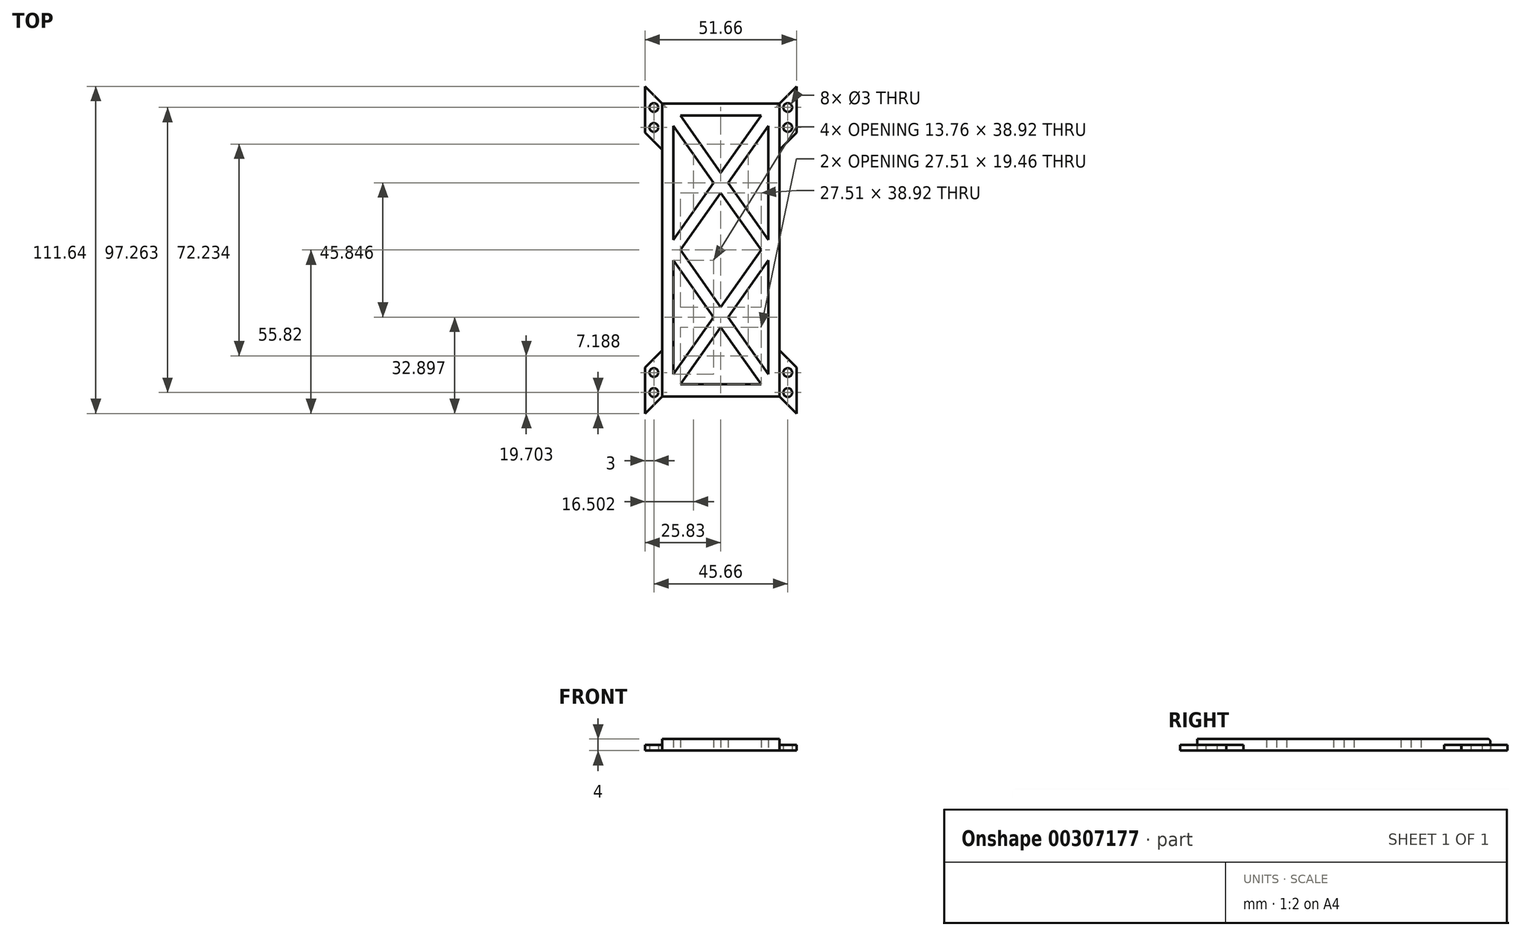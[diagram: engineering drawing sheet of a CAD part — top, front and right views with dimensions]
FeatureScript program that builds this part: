
annotation { "Feature Type Name" : "Feature", "Feature Type Description" : "" }
export const myFeature = defineFeature(function(context is Context, id is Id, definition is map)
    precondition{}
    {
        {
            var Q0;
            Q0=qCreatedBy(makeId("Top.planeOp"),FACE);
            var sketch = newSketch(context, id + "F0", { "sketchPlane" : qUnion([Q0])});
            skLineSegment(sketch, "E0.bottom", {"start": v(20, 50) * mm, "end": v(-20, 50) * mm});
            skLineSegment(sketch, "E0.top", {"start": v(20, -50) * mm, "end": v(-20, -50) * mm});
            skLineSegment(sketch, "E0.left", {"start": v(20, 50) * mm, "end": v(20, -50) * mm});
            skLineSegment(sketch, "E0.right", {"start": v(-20, 50) * mm, "end": v(-20, -50) * mm});
            skPoint(sketch, "E0.middle", {"position": v(0, 0) * mm});
            skLineSegment(sketch, "E1.bottom", {"start": v(16.2, -45.85) * mm, "end": v(-16.2, -45.85) * mm});
            skLineSegment(sketch, "E1.top", {"start": v(16.2, 45.85) * mm, "end": v(-16.2, 45.85) * mm});
            skLineSegment(sketch, "E1.left", {"start": v(16.2, -45.85) * mm, "end": v(16.2, 45.85) * mm});
            skLineSegment(sketch, "E1.right", {"start": v(-16.2, -45.85) * mm, "end": v(-16.2, 45.85) * mm});
            skLineSegment(sketch, "E2", {"start": v(-16.2, 0) * mm, "end": v(16.2, 0) * mm});
            skLineSegment(sketch, "E3", {"start": v(16.2, 0) * mm, "end": v(-16.2, 45.85) * mm});
            skLineSegment(sketch, "E4", {"start": v(-16.2, 0) * mm, "end": v(16.2, 45.85) * mm});
            skLineSegment(sketch, "E5", {"start": v(-16.2, 0) * mm, "end": v(16.2, -45.85) * mm});
            skLineSegment(sketch, "E6", {"start": v(16.2, 0) * mm, "end": v(-16.2, -45.85) * mm});
            skLineSegment(sketch, "E7.0", {"start": v(17.84, 1.15) * mm, "end": v(-14.57, 47) * mm});
            skLineSegment(sketch, "E8.0", {"start": v(14.57, -1.15) * mm, "end": v(-17.84, 44.7) * mm});
            skLineSegment(sketch, "E9.0", {"start": v(-14.57, -1.15) * mm, "end": v(17.84, 44.7) * mm});
            skLineSegment(sketch, "E10.0", {"start": v(-17.84, 1.15) * mm, "end": v(14.57, 47) * mm});
            skLineSegment(sketch, "E11.0", {"start": v(-16.2, -2) * mm, "end": v(16.2, -2) * mm});
            skLineSegment(sketch, "E12.0", {"start": v(-16.2, 2) * mm, "end": v(16.2, 2) * mm});
            skLineSegment(sketch, "E13.0", {"start": v(14.57, 1.15) * mm, "end": v(-17.84, -44.7) * mm});
            skLineSegment(sketch, "E14.0", {"start": v(17.84, -1.15) * mm, "end": v(-14.57, -47) * mm});
            skLineSegment(sketch, "E15.0", {"start": v(-17.84, -1.15) * mm, "end": v(14.57, -47) * mm});
            skLineSegment(sketch, "E16.0", {"start": v(-14.57, 1.15) * mm, "end": v(17.84, -44.7) * mm});
            skLineSegment(sketch, "E17", {"start": v(20, 50) * mm, "end": v(25.83, 55.82) * mm});
            skLineSegment(sketch, "E18", {"start": v(25.83, 55.82) * mm, "end": v(25.83, 40.05) * mm});
            skLineSegment(sketch, "E19", {"start": v(25.83, 40.05) * mm, "end": v(20, 34.24) * mm});
            skLineSegment(sketch, "E20.MirrorCS", {"start": v(25.83, -40.05) * mm, "end": v(20, -34.24) * mm});
            skLineSegment(sketch, "E21.MirrorCS", {"start": v(25.83, -55.82) * mm, "end": v(25.83, -40.05) * mm});
            skLineSegment(sketch, "E22.MirrorCS", {"start": v(20, -50) * mm, "end": v(25.83, -55.82) * mm});
            skLineSegment(sketch, "E23", {"start": v(0, 50) * mm, "end": v(0, -45.85) * mm, "construction": true});
            skLineSegment(sketch, "E24.MirrorCS", {"start": v(-25.83, 40.05) * mm, "end": v(-20, 34.24) * mm});
            skLineSegment(sketch, "E25.MirrorCS", {"start": v(-25.83, 55.82) * mm, "end": v(-25.83, 40.05) * mm});
            skLineSegment(sketch, "E26.MirrorCS", {"start": v(-20, 50) * mm, "end": v(-25.83, 55.82) * mm});
            skLineSegment(sketch, "E27.MirrorCS", {"start": v(-25.83, -40.05) * mm, "end": v(-20, -34.24) * mm});
            skLineSegment(sketch, "E28.MirrorCS", {"start": v(-25.83, -55.82) * mm, "end": v(-25.83, -40.05) * mm});
            skLineSegment(sketch, "E29.MirrorCS", {"start": v(-20, -50) * mm, "end": v(-25.83, -55.82) * mm});
            skPoint(sketch, "E30", {"position": v(22.83, 48.63) * mm});
            skPoint(sketch, "E31", {"position": v(22.83, 41.82) * mm});
            skPoint(sketch, "E32.MirrorP", {"position": v(-22.83, 48.63) * mm});
            skPoint(sketch, "E33.MirrorP", {"position": v(-22.83, 41.82) * mm});
            skPoint(sketch, "E34.MirrorP", {"position": v(22.83, -48.63) * mm});
            skPoint(sketch, "E35.MirrorP", {"position": v(22.83, -41.82) * mm});
            skPoint(sketch, "E36.MirrorP", {"position": v(-22.83, -41.82) * mm});
            skPoint(sketch, "E37.MirrorP", {"position": v(-22.83, -48.63) * mm});
            skSolve(sketch);
        }
        {
            var Q0;
            {var subQ0=sQuery(id+"F0.wireOp",EDGE,"E12.0");var subQ1=sQuery(id+"F0.wireOp",EDGE,"E3");var subQ2=makeQuery(id+"F0.imprint","INTERSECT",VERTEX,{"derivedFrom":[subQ1,subQ0]});Q0=makeQuery(id+"F0.imprint","IMPRINT",FACE,{"disambiguationData":[TD([[makeQuery(id+"F0.imprint","IMPRINT",EDGE,{"disambiguationData":[TD([[subQ2,-1.0]])],"derivedFrom":subQ1}),1.0]])]});}
            var Q1;
            {var subQ5=sQuery(id+"F0.wireOp",EDGE,"E1.left");var subQ7=sQuery(id+"F0.wireOp",EDGE,"E12.0");var subQ9=makeQuery(id+"F0.imprint","INTERSECT",VERTEX,{"derivedFrom":[subQ5,subQ7]});Q1=makeQuery(id+"F0.imprint","IMPRINT",FACE,{"disambiguationData":[TD([[makeQuery(id+"F0.imprint","IMPRINT",EDGE,{"disambiguationData":[TD([[subQ9,-1.0]])],"derivedFrom":subQ5}),1.0]])]});}
            var Q2;
            {var subQ0=sQuery(id+"F0.wireOp",EDGE,"E4");var subQ5=sQuery(id+"F0.wireOp",EDGE,"E7.0");var subQ6=makeQuery(id+"F0.imprint","INTERSECT",VERTEX,{"derivedFrom":[subQ0,subQ5]});Q2=makeQuery(id+"F0.imprint","IMPRINT",FACE,{"disambiguationData":[TD([[makeQuery(id+"F0.imprint","IMPRINT",EDGE,{"disambiguationData":[TD([[subQ6,-1.0]])],"derivedFrom":subQ5}),-1.0]])]});}
            var Q3;
            {var subQ0=sQuery(id+"F0.wireOp",EDGE,"E4");var subQ5=sQuery(id+"F0.wireOp",EDGE,"E7.0");var subQ7=makeQuery(id+"F0.imprint","INTERSECT",VERTEX,{"derivedFrom":[subQ0,subQ5]});Q3=makeQuery(id+"F0.imprint","IMPRINT",FACE,{"disambiguationData":[TD([[makeQuery(id+"F0.imprint","IMPRINT",EDGE,{"disambiguationData":[TD([[subQ7,1.0]])],"derivedFrom":subQ5}),-1.0]])]});}
            var Q4;
            {var subQ0=sQuery(id+"F0.wireOp",EDGE,"E9.0");var subQ1=sQuery(id+"F0.wireOp",EDGE,"E3");var subQ2=makeQuery(id+"F0.imprint","INTERSECT",VERTEX,{"derivedFrom":[subQ1,subQ0]});Q4=makeQuery(id+"F0.imprint","IMPRINT",FACE,{"disambiguationData":[TD([[makeQuery(id+"F0.imprint","IMPRINT",EDGE,{"disambiguationData":[TD([[subQ2,-1.0]])],"derivedFrom":subQ1}),-1.0]])]});}
            var Q5;
            {var subQ0=sQuery(id+"F0.wireOp",EDGE,"E4");var subQ1=sQuery(id+"F0.wireOp",EDGE,"E3");var subQ2=makeQuery(id+"F0.imprint","INTERSECT",VERTEX,{"derivedFrom":[subQ1,subQ0]});Q5=makeQuery(id+"F0.imprint","IMPRINT",FACE,{"disambiguationData":[TD([[makeQuery(id+"F0.imprint","IMPRINT",EDGE,{"disambiguationData":[TD([[subQ2,-1.0]])],"derivedFrom":subQ1}),-1.0]])]});}
            var Q6;
            {var subQ0=sQuery(id+"F0.wireOp",EDGE,"E4");var subQ1=sQuery(id+"F0.wireOp",EDGE,"E3");var subQ2=makeQuery(id+"F0.imprint","INTERSECT",VERTEX,{"derivedFrom":[subQ1,subQ0]});Q6=makeQuery(id+"F0.imprint","IMPRINT",FACE,{"disambiguationData":[TD([[makeQuery(id+"F0.imprint","IMPRINT",EDGE,{"disambiguationData":[TD([[subQ2,-1.0]])],"derivedFrom":subQ1}),1.0]])]});}
            var Q7;
            {var subQ0=sQuery(id+"F0.wireOp",EDGE,"E9.0");var subQ1=sQuery(id+"F0.wireOp",EDGE,"E3");var subQ2=makeQuery(id+"F0.imprint","INTERSECT",VERTEX,{"derivedFrom":[subQ1,subQ0]});Q7=makeQuery(id+"F0.imprint","IMPRINT",FACE,{"disambiguationData":[TD([[makeQuery(id+"F0.imprint","IMPRINT",EDGE,{"disambiguationData":[TD([[subQ2,-1.0]])],"derivedFrom":subQ1}),1.0]])]});}
            var Q8;
            {var subQ1=sQuery(id+"F0.wireOp",EDGE,"E1.right");var subQ3=sQuery(id+"F0.wireOp",EDGE,"E8.0");var subQ4=makeQuery(id+"F0.imprint","INTERSECT",VERTEX,{"derivedFrom":[subQ1,subQ3]});Q8=makeQuery(id+"F0.imprint","IMPRINT",FACE,{"disambiguationData":[TD([[makeQuery(id+"F0.imprint","IMPRINT",EDGE,{"disambiguationData":[TD([[subQ4,1.0]])],"derivedFrom":subQ3}),-1.0]])]});}
            var Q9;
            {var subQ1=sQuery(id+"F0.wireOp",EDGE,"E1.top");var subQ3=sQuery(id+"F0.wireOp",EDGE,"E7.0");var subQ4=makeQuery(id+"F0.imprint","INTERSECT",VERTEX,{"derivedFrom":[subQ1,subQ3]});Q9=makeQuery(id+"F0.imprint","IMPRINT",FACE,{"disambiguationData":[TD([[makeQuery(id+"F0.imprint","IMPRINT",EDGE,{"disambiguationData":[TD([[subQ4,1.0]])],"derivedFrom":subQ3}),1.0]])]});}
            var Q10;
            {var subQ5=sQuery(id+"F0.wireOp",EDGE,"E12.0");var subQ6=sQuery(id+"F0.wireOp",EDGE,"E1.right");var subQ7=makeQuery(id+"F0.imprint","INTERSECT",VERTEX,{"derivedFrom":[subQ6,subQ5]});Q10=makeQuery(id+"F0.imprint","IMPRINT",FACE,{"disambiguationData":[TD([[makeQuery(id+"F0.imprint","IMPRINT",EDGE,{"disambiguationData":[TD([[subQ7,-1.0]])],"derivedFrom":subQ6}),-1.0]])]});}
            var Q11;
            {var subQ0=sQuery(id+"F0.wireOp",EDGE,"E12.0");var subQ1=sQuery(id+"F0.wireOp",EDGE,"E4");var subQ2=makeQuery(id+"F0.imprint","INTERSECT",VERTEX,{"derivedFrom":[subQ1,subQ0]});Q11=makeQuery(id+"F0.imprint","IMPRINT",FACE,{"disambiguationData":[TD([[makeQuery(id+"F0.imprint","IMPRINT",EDGE,{"disambiguationData":[TD([[subQ2,-1.0]])],"derivedFrom":subQ1}),-1.0]])]});}
            var Q12;
            {var subQ0=sQuery(id+"F0.wireOp",EDGE,"E11.0");var subQ1=sQuery(id+"F0.wireOp",EDGE,"E5");var subQ2=makeQuery(id+"F0.imprint","INTERSECT",VERTEX,{"derivedFrom":[subQ1,subQ0]});Q12=makeQuery(id+"F0.imprint","IMPRINT",FACE,{"disambiguationData":[TD([[makeQuery(id+"F0.imprint","IMPRINT",EDGE,{"disambiguationData":[TD([[subQ2,-1.0]])],"derivedFrom":subQ1}),1.0]])]});}
            var Q13;
            {var subQ0=sQuery(id+"F0.wireOp",EDGE,"E11.0");var subQ1=sQuery(id+"F0.wireOp",EDGE,"E1.right");var subQ2=makeQuery(id+"F0.imprint","INTERSECT",VERTEX,{"derivedFrom":[subQ1,subQ0]});Q13=makeQuery(id+"F0.imprint","IMPRINT",FACE,{"disambiguationData":[TD([[makeQuery(id+"F0.imprint","IMPRINT",EDGE,{"disambiguationData":[TD([[subQ2,1.0]])],"derivedFrom":subQ1}),-1.0]])]});}
            var Q14;
            {var subQ31=sQuery(id+"F0.wireOp",EDGE,"E0.bottom");Q14=makeQuery(id+"F0.imprint","IMPRINT",FACE,{"disambiguationData":[TD([[makeQuery(id+"F0.imprint","IMPRINT",EDGE,{"derivedFrom":subQ31}),1.0]])]});}
            var Q15;
            {var subQ0=sQuery(id+"F0.wireOp",EDGE,"E11.0");var subQ1=sQuery(id+"F0.wireOp",EDGE,"E6");var subQ2=makeQuery(id+"F0.imprint","INTERSECT",VERTEX,{"derivedFrom":[subQ1,subQ0]});Q15=makeQuery(id+"F0.imprint","IMPRINT",FACE,{"disambiguationData":[TD([[makeQuery(id+"F0.imprint","IMPRINT",EDGE,{"disambiguationData":[TD([[subQ2,-1.0]])],"derivedFrom":subQ1}),-1.0]])]});}
            var Q16;
            {var subQ0=sQuery(id+"F0.wireOp",EDGE,"E11.0");var subQ1=sQuery(id+"F0.wireOp",EDGE,"E1.left");var subQ2=makeQuery(id+"F0.imprint","INTERSECT",VERTEX,{"derivedFrom":[subQ1,subQ0]});Q16=makeQuery(id+"F0.imprint","IMPRINT",FACE,{"disambiguationData":[TD([[makeQuery(id+"F0.imprint","IMPRINT",EDGE,{"disambiguationData":[TD([[subQ2,1.0]])],"derivedFrom":subQ1}),1.0]])]});}
            var Q17;
            {var subQ0=sQuery(id+"F0.wireOp",EDGE,"E13.0");var subQ1=sQuery(id+"F0.wireOp",EDGE,"E5");var subQ2=makeQuery(id+"F0.imprint","INTERSECT",VERTEX,{"derivedFrom":[subQ1,subQ0]});Q17=makeQuery(id+"F0.imprint","IMPRINT",FACE,{"disambiguationData":[TD([[makeQuery(id+"F0.imprint","IMPRINT",EDGE,{"disambiguationData":[TD([[subQ2,-1.0]])],"derivedFrom":subQ1}),1.0]])]});}
            var Q18;
            {var subQ0=sQuery(id+"F0.wireOp",EDGE,"E6");var subQ1=sQuery(id+"F0.wireOp",EDGE,"E5");var subQ2=makeQuery(id+"F0.imprint","INTERSECT",VERTEX,{"derivedFrom":[subQ1,subQ0]});Q18=makeQuery(id+"F0.imprint","IMPRINT",FACE,{"disambiguationData":[TD([[makeQuery(id+"F0.imprint","IMPRINT",EDGE,{"disambiguationData":[TD([[subQ2,-1.0]])],"derivedFrom":subQ1}),1.0]])]});}
            var Q19;
            {var subQ0=sQuery(id+"F0.wireOp",EDGE,"E6");var subQ1=sQuery(id+"F0.wireOp",EDGE,"E5");var subQ2=makeQuery(id+"F0.imprint","INTERSECT",VERTEX,{"derivedFrom":[subQ1,subQ0]});Q19=makeQuery(id+"F0.imprint","IMPRINT",FACE,{"disambiguationData":[TD([[makeQuery(id+"F0.imprint","IMPRINT",EDGE,{"disambiguationData":[TD([[subQ2,-1.0]])],"derivedFrom":subQ1}),-1.0]])]});}
            var Q20;
            {var subQ0=sQuery(id+"F0.wireOp",EDGE,"E13.0");var subQ1=sQuery(id+"F0.wireOp",EDGE,"E5");var subQ2=makeQuery(id+"F0.imprint","INTERSECT",VERTEX,{"derivedFrom":[subQ1,subQ0]});Q20=makeQuery(id+"F0.imprint","IMPRINT",FACE,{"disambiguationData":[TD([[makeQuery(id+"F0.imprint","IMPRINT",EDGE,{"disambiguationData":[TD([[subQ2,-1.0]])],"derivedFrom":subQ1}),-1.0]])]});}
            var Q21;
            {var subQ1=sQuery(id+"F0.wireOp",EDGE,"E1.right");var subQ3=sQuery(id+"F0.wireOp",EDGE,"E13.0");var subQ4=makeQuery(id+"F0.imprint","INTERSECT",VERTEX,{"derivedFrom":[subQ1,subQ3]});Q21=makeQuery(id+"F0.imprint","IMPRINT",FACE,{"disambiguationData":[TD([[makeQuery(id+"F0.imprint","IMPRINT",EDGE,{"disambiguationData":[TD([[subQ4,1.0]])],"derivedFrom":subQ3}),1.0]])]});}
            var Q22;
            {var subQ1=sQuery(id+"F0.wireOp",EDGE,"E1.bottom");var subQ3=sQuery(id+"F0.wireOp",EDGE,"E14.0");var subQ4=makeQuery(id+"F0.imprint","INTERSECT",VERTEX,{"derivedFrom":[subQ1,subQ3]});Q22=makeQuery(id+"F0.imprint","IMPRINT",FACE,{"disambiguationData":[TD([[makeQuery(id+"F0.imprint","IMPRINT",EDGE,{"disambiguationData":[TD([[subQ4,1.0]])],"derivedFrom":subQ3}),-1.0]])]});}
            var Q23;
            {var subQ0=sQuery(id+"F0.wireOp",EDGE,"E5");var subQ5=sQuery(id+"F0.wireOp",EDGE,"E14.0");var subQ6=makeQuery(id+"F0.imprint","INTERSECT",VERTEX,{"derivedFrom":[subQ0,subQ5]});Q23=makeQuery(id+"F0.imprint","IMPRINT",FACE,{"disambiguationData":[TD([[makeQuery(id+"F0.imprint","IMPRINT",EDGE,{"disambiguationData":[TD([[subQ6,1.0]])],"derivedFrom":subQ5}),1.0]])]});}
            var Q24;
            {var subQ0=sQuery(id+"F0.wireOp",EDGE,"E5");var subQ5=sQuery(id+"F0.wireOp",EDGE,"E14.0");var subQ6=makeQuery(id+"F0.imprint","INTERSECT",VERTEX,{"derivedFrom":[subQ0,subQ5]});Q24=makeQuery(id+"F0.imprint","IMPRINT",FACE,{"disambiguationData":[TD([[makeQuery(id+"F0.imprint","IMPRINT",EDGE,{"disambiguationData":[TD([[subQ6,-1.0]])],"derivedFrom":subQ5}),1.0]])]});}
            var Q25;
            {var subQ1=sQuery(id+"F0.wireOp",EDGE,"E1.left");var subQ3=sQuery(id+"F0.wireOp",EDGE,"E11.0");var subQ4=makeQuery(id+"F0.imprint","INTERSECT",VERTEX,{"derivedFrom":[subQ1,subQ3]});Q25=makeQuery(id+"F0.imprint","IMPRINT",FACE,{"disambiguationData":[TD([[makeQuery(id+"F0.imprint","IMPRINT",EDGE,{"disambiguationData":[TD([[subQ4,1.0]])],"derivedFrom":subQ3}),1.0]])]});}
            var Q26;
            {var subQ1=sQuery(id+"F0.wireOp",EDGE,"E1.left");var subQ3=sQuery(id+"F0.wireOp",EDGE,"E12.0");var subQ4=makeQuery(id+"F0.imprint","INTERSECT",VERTEX,{"derivedFrom":[subQ1,subQ3]});Q26=makeQuery(id+"F0.imprint","IMPRINT",FACE,{"disambiguationData":[TD([[makeQuery(id+"F0.imprint","IMPRINT",EDGE,{"disambiguationData":[TD([[subQ4,1.0]])],"derivedFrom":subQ3}),-1.0]])]});}
            var Q27;
            {var subQ0=sQuery(id+"F0.wireOp",EDGE,"E6");var subQ5=sQuery(id+"F0.wireOp",EDGE,"E11.0");var subQ6=makeQuery(id+"F0.imprint","INTERSECT",VERTEX,{"derivedFrom":[subQ0,subQ5]});Q27=makeQuery(id+"F0.imprint","IMPRINT",FACE,{"disambiguationData":[TD([[makeQuery(id+"F0.imprint","IMPRINT",EDGE,{"disambiguationData":[TD([[subQ6,1.0]])],"derivedFrom":subQ5}),1.0]])]});}
            var Q28;
            {var subQ0=sQuery(id+"F0.wireOp",EDGE,"E3");var subQ5=sQuery(id+"F0.wireOp",EDGE,"E12.0");var subQ7=makeQuery(id+"F0.imprint","INTERSECT",VERTEX,{"derivedFrom":[subQ0,subQ5]});Q28=makeQuery(id+"F0.imprint","IMPRINT",FACE,{"disambiguationData":[TD([[makeQuery(id+"F0.imprint","IMPRINT",EDGE,{"disambiguationData":[TD([[subQ7,1.0]])],"derivedFrom":subQ5}),-1.0]])]});}
            var Q29;
            {var subQ0=sQuery(id+"F0.wireOp",EDGE,"E5");var subQ5=sQuery(id+"F0.wireOp",EDGE,"E11.0");var subQ6=makeQuery(id+"F0.imprint","INTERSECT",VERTEX,{"derivedFrom":[subQ0,subQ5]});Q29=makeQuery(id+"F0.imprint","IMPRINT",FACE,{"disambiguationData":[TD([[makeQuery(id+"F0.imprint","IMPRINT",EDGE,{"disambiguationData":[TD([[subQ6,-1.0]])],"derivedFrom":subQ5}),1.0]])]});}
            var Q30;
            {var subQ0=sQuery(id+"F0.wireOp",EDGE,"E4");var subQ5=sQuery(id+"F0.wireOp",EDGE,"E12.0");var subQ6=makeQuery(id+"F0.imprint","INTERSECT",VERTEX,{"derivedFrom":[subQ0,subQ5]});Q30=makeQuery(id+"F0.imprint","IMPRINT",FACE,{"disambiguationData":[TD([[makeQuery(id+"F0.imprint","IMPRINT",EDGE,{"disambiguationData":[TD([[subQ6,-1.0]])],"derivedFrom":subQ5}),-1.0]])]});}
            var Q31;
            {var subQ1=sQuery(id+"F0.wireOp",EDGE,"E1.right");var subQ3=sQuery(id+"F0.wireOp",EDGE,"E12.0");var subQ4=makeQuery(id+"F0.imprint","INTERSECT",VERTEX,{"derivedFrom":[subQ1,subQ3]});Q31=makeQuery(id+"F0.imprint","IMPRINT",FACE,{"disambiguationData":[TD([[makeQuery(id+"F0.imprint","IMPRINT",EDGE,{"disambiguationData":[TD([[subQ4,-1.0]])],"derivedFrom":subQ3}),-1.0]])]});}
            var Q32;
            {var subQ1=sQuery(id+"F0.wireOp",EDGE,"E1.right");var subQ3=sQuery(id+"F0.wireOp",EDGE,"E11.0");var subQ4=makeQuery(id+"F0.imprint","INTERSECT",VERTEX,{"derivedFrom":[subQ1,subQ3]});Q32=makeQuery(id+"F0.imprint","IMPRINT",FACE,{"disambiguationData":[TD([[makeQuery(id+"F0.imprint","IMPRINT",EDGE,{"disambiguationData":[TD([[subQ4,-1.0]])],"derivedFrom":subQ3}),1.0]])]});}
            extrude(context, id + "F1", {"entities" : qUnion([Q0, Q1, Q2, Q3, Q4, Q5, Q6, Q7, Q8, Q9, Q10, Q11, Q12, Q13, Q14, Q15, Q16, Q17, Q18, Q19, Q20, Q21, Q22, Q23, Q24, Q25, Q26, Q27, Q28, Q29, Q30, Q31, Q32]), "depth" : 4 * mm});
        }
        {
            var Q0;
            {var subQ0=sQuery(id+"F0.wireOp",EDGE,"E17");Q0=makeQuery(id+"F0.imprint","IMPRINT",FACE,{"disambiguationData":[TD([[makeQuery(id+"F0.imprint","IMPRINT",EDGE,{"derivedFrom":subQ0}),-1.0]])]});}
            var Q1;
            {var subQ2=sQuery(id+"F0.wireOp",EDGE,"E24.MirrorCS");Q1=makeQuery(id+"F0.imprint","IMPRINT",FACE,{"disambiguationData":[TD([[makeQuery(id+"F0.imprint","IMPRINT",EDGE,{"derivedFrom":subQ2}),1.0]])]});}
            var Q2;
            {var subQ2=sQuery(id+"F0.wireOp",EDGE,"E27.MirrorCS");Q2=makeQuery(id+"F0.imprint","IMPRINT",FACE,{"disambiguationData":[TD([[makeQuery(id+"F0.imprint","IMPRINT",EDGE,{"derivedFrom":subQ2}),-1.0]])]});}
            var Q3;
            {var subQ0=sQuery(id+"F0.wireOp",EDGE,"E22.MirrorCS");Q3=makeQuery(id+"F0.imprint","IMPRINT",FACE,{"disambiguationData":[TD([[makeQuery(id+"F0.imprint","IMPRINT",EDGE,{"derivedFrom":subQ0}),1.0]])]});}
            extrude(context, id + "F2", {"entities" : qUnion([Q0, Q1, Q2, Q3]), "operationType" : NewBodyOperationType.ADD, "depth" : 2 * mm});
        }
        {
            var Q0;
            Q0=sQuery(id+"F0.wireOp",VERTEX,"E30");
            var Q1;
            Q1=sQuery(id+"F0.wireOp",VERTEX,"E31");
            var Q2;
            Q2=sQuery(id+"F0.wireOp",VERTEX,"E32.MirrorP");
            var Q3;
            Q3=sQuery(id+"F0.wireOp",VERTEX,"E33.MirrorP");
            var Q4;
            Q4=sQuery(id+"F0.wireOp",VERTEX,"E36.MirrorP");
            var Q5;
            Q5=sQuery(id+"F0.wireOp",VERTEX,"E37.MirrorP");
            var Q6;
            Q6=sQuery(id+"F0.wireOp",VERTEX,"E35.MirrorP");
            var Q7;
            Q7=sQuery(id+"F0.wireOp",VERTEX,"E34.MirrorP");
            var Q8;
            Q8=makeQuery(id+"F1.opExtrude","SWEPT_BODY",BODY,{"disambiguationData":[OSD([sQuery(id+"F0.wireOp",EDGE,"E0.bottom"),sQuery(id+"F0.wireOp",EDGE,"E0.top"),sQuery(id+"F0.wireOp",EDGE,"E0.left"),sQuery(id+"F0.wireOp",EDGE,"E0.right"),sQuery(id+"F0.wireOp",EDGE,"E1.bottom"),sQuery(id+"F0.wireOp",EDGE,"E1.top"),sQuery(id+"F0.wireOp",EDGE,"E1.left"),sQuery(id+"F0.wireOp",EDGE,"E1.right"),sQuery(id+"F0.wireOp",EDGE,"E7.0"),sQuery(id+"F0.wireOp",EDGE,"E8.0"),sQuery(id+"F0.wireOp",EDGE,"E9.0"),sQuery(id+"F0.wireOp",EDGE,"E10.0"),sQuery(id+"F0.wireOp",EDGE,"E13.0"),sQuery(id+"F0.wireOp",EDGE,"E14.0"),sQuery(id+"F0.wireOp",EDGE,"E15.0"),sQuery(id+"F0.wireOp",EDGE,"E16.0")])]});
            hole(context, id + "F3", {"style" : HoleStyle.SIMPLE, "endStyle" : HoleEndStyle.THROUGH, "oppositeDirection" : true, "holeDiameter" : 3 * mm, "tappedDepth" : 12 * mm, "tapClearance" : 3, "locations" : qUnion([Q0, Q1, Q2, Q3, Q4, Q5, Q6, Q7]), "scope" : qUnion([Q8])});
        }
        {
            var Q0;
            Q0=makeQuery(id+"F1.opExtrude","CAP_EDGE",EDGE,{"disambiguationData":[OSD([sQuery(id+"F0.wireOp",EDGE,"E0.bottom")])],"isStart":false});
            var Q1;
            Q1=makeQuery(id+"F1.opExtrude","CAP_EDGE",EDGE,{"disambiguationData":[OSD([sQuery(id+"F0.wireOp",EDGE,"E0.bottom")])],"isStart":true});
            fillet(context, id + "F4", {"entities" : qUnion([Q0, Q1]), "radius" : 1 * mm, "tangentPropagation" : true, "allowEdgeOverflow" : false});
        }
    });
